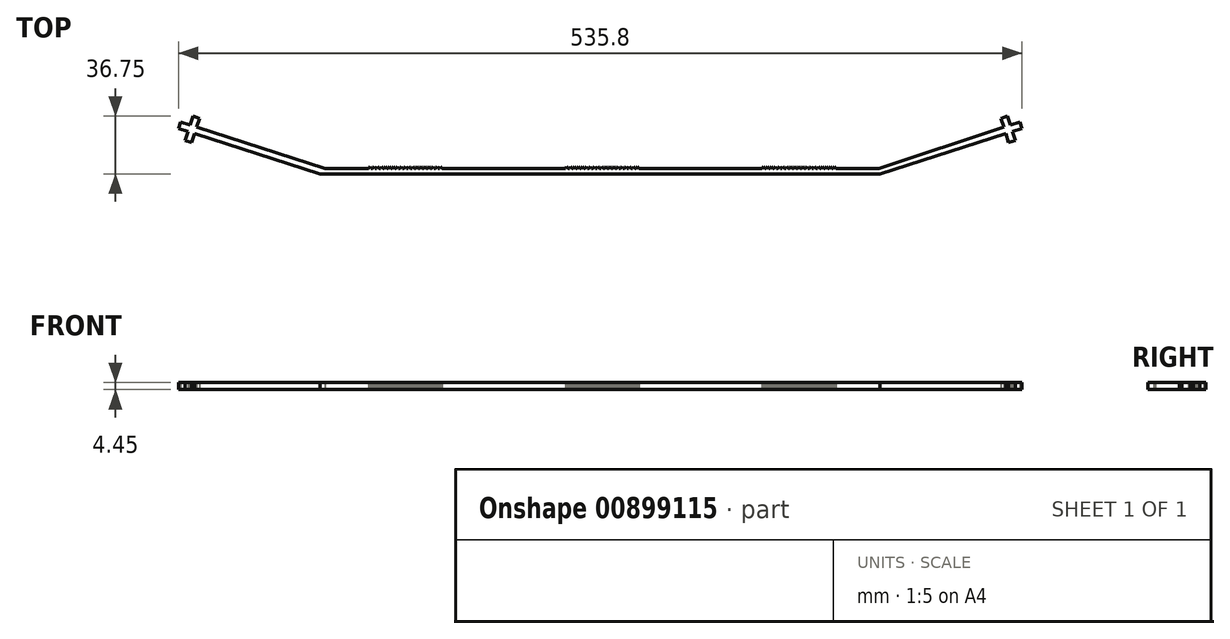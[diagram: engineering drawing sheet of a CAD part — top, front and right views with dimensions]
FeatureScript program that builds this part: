
annotation { "Feature Type Name" : "Feature", "Feature Type Description" : "" }
export const myFeature = defineFeature(function(context is Context, id is Id, definition is map)
    precondition{}
    {
        {
            var Q0;
            Q0=qCreatedBy(makeId("Top.planeOp"),FACE);
            var sketch = newSketch(context, id + "F0", { "sketchPlane" : qUnion([Q0])});
            skLineSegment(sketch, "E0", {"start": v(-253.44, 7.28) * mm, "end": v(102.16, 7.28) * mm});
            skLineSegment(sketch, "E1", {"start": v(-253.44, 7.28) * mm, "end": v(-333.25, 32.88) * mm});
            skLineSegment(sketch, "E2", {"start": v(-333.25, 32.88) * mm, "end": v(-335.04, 27.33) * mm});
            skLineSegment(sketch, "E3", {"start": v(-335.04, 27.33) * mm, "end": v(-339.27, 28.69) * mm});
            skLineSegment(sketch, "E4", {"start": v(-339.27, 28.69) * mm, "end": v(-337.5, 34.24) * mm});
            skLineSegment(sketch, "E5", {"start": v(-337.5, 34.24) * mm, "end": v(-343.54, 36.18) * mm});
            skLineSegment(sketch, "E6", {"start": v(-343.54, 36.18) * mm, "end": v(-342.18, 40.42) * mm});
            skLineSegment(sketch, "E7", {"start": v(-342.18, 40.42) * mm, "end": v(-336.13, 38.48) * mm});
            skLineSegment(sketch, "E8", {"start": v(-336.13, 38.48) * mm, "end": v(-334.35, 44.03) * mm});
            skLineSegment(sketch, "E9", {"start": v(-334.35, 44.03) * mm, "end": v(-330.11, 42.67) * mm});
            skLineSegment(sketch, "E10", {"start": v(-330.11, 42.67) * mm, "end": v(-331.9, 37.12) * mm});
            skLineSegment(sketch, "E11", {"start": v(-331.9, 37.12) * mm, "end": v(-252.08, 11.52) * mm});
            skLineSegment(sketch, "E12", {"start": v(-250.27, 10.94) * mm, "end": v(-222.78, 10.94) * mm});
            skLineSegment(sketch, "E13", {"start": v(-74.41, 12.08) * mm, "end": v(-73.54, 10.94) * mm});
            skLineSegment(sketch, "E14.MirrorCS", {"start": v(-74.41, 12.08) * mm, "end": v(-75.28, 10.94) * mm});
            skLineSegment(sketch, "E15.trimOffspring", {"start": v(-73.54, 10.94) * mm, "end": v(-72.78, 10.94) * mm});
            skPoint(sketch, "E16.start.orphan", {"position": v(-74.41, 4.9) * mm});
            skLineSegment(sketch, "E17.direction1", {"start": v(-73.54, 10.94) * mm, "end": v(-72.78, 10.94) * mm, "construction": true});
            skLineSegment(sketch, "E18.1.0.0", {"start": v(-71.91, 12.08) * mm, "end": v(-71.04, 10.94) * mm});
            skLineSegment(sketch, "E18.1.0.1", {"start": v(-71.91, 12.08) * mm, "end": v(-72.78, 10.94) * mm});
            skLineSegment(sketch, "E18.2.0.0", {"start": v(-69.41, 12.08) * mm, "end": v(-68.54, 10.94) * mm});
            skLineSegment(sketch, "E18.2.0.1", {"start": v(-69.41, 12.08) * mm, "end": v(-70.28, 10.94) * mm});
            skLineSegment(sketch, "E18.3.0.0", {"start": v(-66.91, 12.08) * mm, "end": v(-66.04, 10.94) * mm});
            skLineSegment(sketch, "E18.3.0.1", {"start": v(-66.91, 12.08) * mm, "end": v(-67.78, 10.94) * mm});
            skLineSegment(sketch, "E18.4.0.0", {"start": v(-64.41, 12.08) * mm, "end": v(-63.54, 10.94) * mm});
            skLineSegment(sketch, "E18.4.0.1", {"start": v(-64.41, 12.08) * mm, "end": v(-65.28, 10.94) * mm});
            skLineSegment(sketch, "E18.5.0.0", {"start": v(-61.91, 12.08) * mm, "end": v(-61.04, 10.94) * mm});
            skLineSegment(sketch, "E18.5.0.1", {"start": v(-61.91, 12.08) * mm, "end": v(-62.78, 10.94) * mm});
            skLineSegment(sketch, "E18.6.0.0", {"start": v(-59.41, 12.08) * mm, "end": v(-58.54, 10.94) * mm});
            skLineSegment(sketch, "E18.6.0.1", {"start": v(-59.41, 12.08) * mm, "end": v(-60.28, 10.94) * mm});
            skLineSegment(sketch, "E18.7.0.0", {"start": v(-56.91, 12.08) * mm, "end": v(-56.04, 10.94) * mm});
            skLineSegment(sketch, "E18.7.0.1", {"start": v(-56.91, 12.08) * mm, "end": v(-57.78, 10.94) * mm});
            skLineSegment(sketch, "E18.8.0.0", {"start": v(-54.41, 12.08) * mm, "end": v(-53.54, 10.94) * mm});
            skLineSegment(sketch, "E18.8.0.1", {"start": v(-54.41, 12.08) * mm, "end": v(-55.28, 10.94) * mm});
            skLineSegment(sketch, "E18.9.0.0", {"start": v(-51.91, 12.08) * mm, "end": v(-51.04, 10.94) * mm});
            skLineSegment(sketch, "E18.9.0.1", {"start": v(-51.91, 12.08) * mm, "end": v(-52.78, 10.94) * mm});
            skLineSegment(sketch, "E19.1.0.0", {"start": v(-76.91, 12.08) * mm, "end": v(-77.78, 10.94) * mm});
            skLineSegment(sketch, "E19.1.0.1", {"start": v(-76.91, 12.08) * mm, "end": v(-76.04, 10.94) * mm});
            skLineSegment(sketch, "E19.2.0.0", {"start": v(-79.41, 12.08) * mm, "end": v(-80.28, 10.94) * mm});
            skLineSegment(sketch, "E19.2.0.1", {"start": v(-79.41, 12.08) * mm, "end": v(-78.54, 10.94) * mm});
            skLineSegment(sketch, "E19.3.0.0", {"start": v(-81.91, 12.08) * mm, "end": v(-82.78, 10.94) * mm});
            skLineSegment(sketch, "E19.3.0.1", {"start": v(-81.91, 12.08) * mm, "end": v(-81.04, 10.94) * mm});
            skLineSegment(sketch, "E19.4.0.0", {"start": v(-84.41, 12.08) * mm, "end": v(-85.28, 10.94) * mm});
            skLineSegment(sketch, "E19.4.0.1", {"start": v(-84.41, 12.08) * mm, "end": v(-83.54, 10.94) * mm});
            skLineSegment(sketch, "E19.5.0.0", {"start": v(-86.91, 12.08) * mm, "end": v(-87.78, 10.94) * mm});
            skLineSegment(sketch, "E19.5.0.1", {"start": v(-86.91, 12.08) * mm, "end": v(-86.04, 10.94) * mm});
            skLineSegment(sketch, "E19.6.0.0", {"start": v(-89.41, 12.08) * mm, "end": v(-90.28, 10.94) * mm});
            skLineSegment(sketch, "E19.6.0.1", {"start": v(-89.41, 12.08) * mm, "end": v(-88.54, 10.94) * mm});
            skLineSegment(sketch, "E19.7.0.0", {"start": v(-91.91, 12.08) * mm, "end": v(-92.78, 10.94) * mm});
            skLineSegment(sketch, "E19.7.0.1", {"start": v(-91.91, 12.08) * mm, "end": v(-91.04, 10.94) * mm});
            skLineSegment(sketch, "E19.8.0.0", {"start": v(-94.41, 12.08) * mm, "end": v(-95.28, 10.94) * mm});
            skLineSegment(sketch, "E19.8.0.1", {"start": v(-94.41, 12.08) * mm, "end": v(-93.54, 10.94) * mm});
            skLineSegment(sketch, "E19.9.0.0", {"start": v(-96.91, 12.08) * mm, "end": v(-97.78, 10.94) * mm});
            skLineSegment(sketch, "E19.9.0.1", {"start": v(-96.91, 12.08) * mm, "end": v(-96.04, 10.94) * mm});
            skLineSegment(sketch, "E19.direction1", {"start": v(-75.28, 10.94) * mm, "end": v(-76.04, 10.94) * mm, "construction": true});
            skLineSegment(sketch, "E20.trimOffspring", {"start": v(-96.04, 10.94) * mm, "end": v(-95.28, 10.94) * mm});
            skLineSegment(sketch, "E21.trimOffspring", {"start": v(-93.54, 10.94) * mm, "end": v(-92.78, 10.94) * mm});
            skLineSegment(sketch, "E22.trimOffspring", {"start": v(-91.04, 10.94) * mm, "end": v(-90.28, 10.94) * mm});
            skLineSegment(sketch, "E23.trimOffspring", {"start": v(-86.04, 10.94) * mm, "end": v(-85.28, 10.94) * mm});
            skLineSegment(sketch, "E24.trimOffspring", {"start": v(-88.54, 10.94) * mm, "end": v(-87.78, 10.94) * mm});
            skLineSegment(sketch, "E25.trimOffspring", {"start": v(-83.54, 10.94) * mm, "end": v(-82.78, 10.94) * mm});
            skLineSegment(sketch, "E26.trimOffspring", {"start": v(-81.04, 10.94) * mm, "end": v(-80.28, 10.94) * mm});
            skLineSegment(sketch, "E27.trimOffspring", {"start": v(-78.54, 10.94) * mm, "end": v(-77.78, 10.94) * mm});
            skLineSegment(sketch, "E28.trimOffspring", {"start": v(-76.04, 10.94) * mm, "end": v(-75.28, 10.94) * mm});
            skLineSegment(sketch, "E29.trimOffspring", {"start": v(-71.04, 10.94) * mm, "end": v(-70.28, 10.94) * mm, "construction": true});
            skLineSegment(sketch, "E30.trimOffspring", {"start": v(-71.04, 10.94) * mm, "end": v(-70.28, 10.94) * mm});
            skLineSegment(sketch, "E31.trimOffspring", {"start": v(-68.54, 10.94) * mm, "end": v(-67.78, 10.94) * mm, "construction": true});
            skLineSegment(sketch, "E32.trimOffspring", {"start": v(-68.54, 10.94) * mm, "end": v(-67.78, 10.94) * mm});
            skLineSegment(sketch, "E33.trimOffspring", {"start": v(-66.04, 10.94) * mm, "end": v(-65.28, 10.94) * mm, "construction": true});
            skLineSegment(sketch, "E34.trimOffspring", {"start": v(-63.54, 10.94) * mm, "end": v(-62.78, 10.94) * mm, "construction": true});
            skLineSegment(sketch, "E35.trimOffspring", {"start": v(-63.54, 10.94) * mm, "end": v(-62.78, 10.94) * mm});
            skLineSegment(sketch, "E36", {"start": v(-66.04, 10.94) * mm, "end": v(-65.28, 10.94) * mm});
            skLineSegment(sketch, "E37.trimOffspring", {"start": v(-61.04, 10.94) * mm, "end": v(-60.28, 10.94) * mm, "construction": true});
            skLineSegment(sketch, "E38.trimOffspring", {"start": v(-61.04, 10.94) * mm, "end": v(-60.28, 10.94) * mm});
            skLineSegment(sketch, "E39.trimOffspring", {"start": v(-58.54, 10.94) * mm, "end": v(-57.78, 10.94) * mm, "construction": true});
            skLineSegment(sketch, "E40.trimOffspring", {"start": v(-58.54, 10.94) * mm, "end": v(-57.78, 10.94) * mm});
            skLineSegment(sketch, "E41.trimOffspring", {"start": v(-56.04, 10.94) * mm, "end": v(-55.28, 10.94) * mm, "construction": true});
            skLineSegment(sketch, "E42.trimOffspring", {"start": v(-56.04, 10.94) * mm, "end": v(-55.28, 10.94) * mm});
            skLineSegment(sketch, "E43.trimOffspring", {"start": v(-53.54, 10.94) * mm, "end": v(-52.78, 10.94) * mm, "construction": true});
            skLineSegment(sketch, "E44.trimOffspring", {"start": v(-53.54, 10.94) * mm, "end": v(-52.78, 10.94) * mm});
            skLineSegment(sketch, "E45.trimOffspring", {"start": v(-51.04, 10.94) * mm, "end": v(-48.54, 10.94) * mm, "construction": true});
            skLineSegment(sketch, "E46.trimOffspring", {"start": v(-51.04, 10.94) * mm, "end": v(27.22, 10.94) * mm});
            skLineSegment(sketch, "E47.1.0.0", {"start": v(73.09, 12.08) * mm, "end": v(73.96, 10.94) * mm});
            skLineSegment(sketch, "E47.1.0.1", {"start": v(73.09, 12.08) * mm, "end": v(72.22, 10.94) * mm});
            skLineSegment(sketch, "E47.1.0.2", {"start": v(70.59, 12.08) * mm, "end": v(71.46, 10.94) * mm});
            skLineSegment(sketch, "E47.1.0.3", {"start": v(70.59, 12.08) * mm, "end": v(69.72, 10.94) * mm});
            skLineSegment(sketch, "E47.1.0.4", {"start": v(68.09, 12.08) * mm, "end": v(68.96, 10.94) * mm});
            skLineSegment(sketch, "E47.1.0.5", {"start": v(68.09, 12.08) * mm, "end": v(67.22, 10.94) * mm});
            skLineSegment(sketch, "E47.1.0.6", {"start": v(65.59, 12.08) * mm, "end": v(66.46, 10.94) * mm});
            skLineSegment(sketch, "E47.1.0.7", {"start": v(65.59, 12.08) * mm, "end": v(64.72, 10.94) * mm});
            skLineSegment(sketch, "E47.1.0.8", {"start": v(63.09, 12.08) * mm, "end": v(63.96, 10.94) * mm});
            skLineSegment(sketch, "E47.1.0.9", {"start": v(63.09, 12.08) * mm, "end": v(62.22, 10.94) * mm});
            skLineSegment(sketch, "E47.1.0.10", {"start": v(60.59, 12.08) * mm, "end": v(61.46, 10.94) * mm});
            skLineSegment(sketch, "E47.1.0.11", {"start": v(60.59, 12.08) * mm, "end": v(59.72, 10.94) * mm});
            skLineSegment(sketch, "E47.1.0.12", {"start": v(58.09, 12.08) * mm, "end": v(58.96, 10.94) * mm});
            skLineSegment(sketch, "E47.1.0.13", {"start": v(58.09, 12.08) * mm, "end": v(57.22, 10.94) * mm});
            skLineSegment(sketch, "E47.1.0.14", {"start": v(55.59, 12.08) * mm, "end": v(56.46, 10.94) * mm});
            skLineSegment(sketch, "E47.1.0.15", {"start": v(55.59, 12.08) * mm, "end": v(54.72, 10.94) * mm});
            skLineSegment(sketch, "E47.1.0.16", {"start": v(53.09, 12.08) * mm, "end": v(53.96, 10.94) * mm});
            skLineSegment(sketch, "E47.1.0.17", {"start": v(53.09, 12.08) * mm, "end": v(52.22, 10.94) * mm});
            skLineSegment(sketch, "E47.1.0.18", {"start": v(50.59, 12.08) * mm, "end": v(51.46, 10.94) * mm});
            skLineSegment(sketch, "E47.1.0.19", {"start": v(50.59, 12.08) * mm, "end": v(49.72, 10.94) * mm});
            skLineSegment(sketch, "E47.1.0.20", {"start": v(48.09, 12.08) * mm, "end": v(48.96, 10.94) * mm});
            skLineSegment(sketch, "E47.1.0.21", {"start": v(48.09, 12.08) * mm, "end": v(47.22, 10.94) * mm});
            skLineSegment(sketch, "E47.1.0.22", {"start": v(45.59, 12.08) * mm, "end": v(46.46, 10.94) * mm});
            skLineSegment(sketch, "E47.1.0.23", {"start": v(45.59, 12.08) * mm, "end": v(44.72, 10.94) * mm});
            skLineSegment(sketch, "E47.1.0.24", {"start": v(43.09, 12.08) * mm, "end": v(43.96, 10.94) * mm});
            skLineSegment(sketch, "E47.1.0.25", {"start": v(43.09, 12.08) * mm, "end": v(42.22, 10.94) * mm});
            skLineSegment(sketch, "E47.1.0.26", {"start": v(40.59, 12.08) * mm, "end": v(41.46, 10.94) * mm});
            skLineSegment(sketch, "E47.1.0.27", {"start": v(40.59, 12.08) * mm, "end": v(39.72, 10.94) * mm});
            skLineSegment(sketch, "E47.1.0.28", {"start": v(38.09, 12.08) * mm, "end": v(38.96, 10.94) * mm});
            skLineSegment(sketch, "E47.1.0.29", {"start": v(38.09, 12.08) * mm, "end": v(37.22, 10.94) * mm});
            skLineSegment(sketch, "E47.1.0.30", {"start": v(35.59, 12.08) * mm, "end": v(36.46, 10.94) * mm});
            skLineSegment(sketch, "E47.1.0.31", {"start": v(35.59, 12.08) * mm, "end": v(34.72, 10.94) * mm});
            skLineSegment(sketch, "E47.1.0.32", {"start": v(33.09, 12.08) * mm, "end": v(33.96, 10.94) * mm});
            skLineSegment(sketch, "E47.1.0.33", {"start": v(33.09, 12.08) * mm, "end": v(32.22, 10.94) * mm});
            skLineSegment(sketch, "E47.1.0.34", {"start": v(30.59, 12.08) * mm, "end": v(31.46, 10.94) * mm});
            skLineSegment(sketch, "E47.1.0.35", {"start": v(30.59, 12.08) * mm, "end": v(29.72, 10.94) * mm});
            skLineSegment(sketch, "E47.1.0.36", {"start": v(28.09, 12.08) * mm, "end": v(28.96, 10.94) * mm});
            skLineSegment(sketch, "E47.1.0.37", {"start": v(28.09, 12.08) * mm, "end": v(27.22, 10.94) * mm});
            skLineSegment(sketch, "E48.1.0.0", {"start": v(-176.91, 12.08) * mm, "end": v(-176.04, 10.94) * mm});
            skLineSegment(sketch, "E48.1.0.1", {"start": v(-176.91, 12.08) * mm, "end": v(-177.78, 10.94) * mm});
            skLineSegment(sketch, "E48.1.0.2", {"start": v(-179.41, 12.08) * mm, "end": v(-178.54, 10.94) * mm});
            skLineSegment(sketch, "E48.1.0.3", {"start": v(-179.41, 12.08) * mm, "end": v(-180.28, 10.94) * mm});
            skLineSegment(sketch, "E48.1.0.4", {"start": v(-181.91, 12.08) * mm, "end": v(-181.04, 10.94) * mm});
            skLineSegment(sketch, "E48.1.0.5", {"start": v(-181.91, 12.08) * mm, "end": v(-182.78, 10.94) * mm});
            skLineSegment(sketch, "E48.1.0.6", {"start": v(-184.41, 12.08) * mm, "end": v(-183.54, 10.94) * mm});
            skLineSegment(sketch, "E48.1.0.7", {"start": v(-184.41, 12.08) * mm, "end": v(-185.28, 10.94) * mm});
            skLineSegment(sketch, "E48.1.0.8", {"start": v(-186.91, 12.08) * mm, "end": v(-186.04, 10.94) * mm});
            skLineSegment(sketch, "E48.1.0.9", {"start": v(-186.91, 12.08) * mm, "end": v(-187.78, 10.94) * mm});
            skLineSegment(sketch, "E48.1.0.10", {"start": v(-189.41, 12.08) * mm, "end": v(-188.54, 10.94) * mm});
            skLineSegment(sketch, "E48.1.0.11", {"start": v(-189.41, 12.08) * mm, "end": v(-190.28, 10.94) * mm});
            skLineSegment(sketch, "E48.1.0.12", {"start": v(-191.91, 12.08) * mm, "end": v(-191.04, 10.94) * mm});
            skLineSegment(sketch, "E48.1.0.13", {"start": v(-191.91, 12.08) * mm, "end": v(-192.78, 10.94) * mm});
            skLineSegment(sketch, "E48.1.0.14", {"start": v(-194.41, 12.08) * mm, "end": v(-193.54, 10.94) * mm});
            skLineSegment(sketch, "E48.1.0.15", {"start": v(-194.41, 12.08) * mm, "end": v(-195.28, 10.94) * mm});
            skLineSegment(sketch, "E48.1.0.16", {"start": v(-196.91, 12.08) * mm, "end": v(-196.04, 10.94) * mm});
            skLineSegment(sketch, "E48.1.0.17", {"start": v(-196.91, 12.08) * mm, "end": v(-197.78, 10.94) * mm});
            skLineSegment(sketch, "E48.1.0.18", {"start": v(-199.41, 12.08) * mm, "end": v(-198.54, 10.94) * mm});
            skLineSegment(sketch, "E48.1.0.19", {"start": v(-199.41, 12.08) * mm, "end": v(-200.28, 10.94) * mm});
            skLineSegment(sketch, "E48.1.0.20", {"start": v(-221.91, 12.08) * mm, "end": v(-222.78, 10.94) * mm});
            skLineSegment(sketch, "E48.1.0.21", {"start": v(-221.91, 12.08) * mm, "end": v(-221.04, 10.94) * mm});
            skLineSegment(sketch, "E48.1.0.22", {"start": v(-219.41, 12.08) * mm, "end": v(-220.28, 10.94) * mm});
            skLineSegment(sketch, "E48.1.0.23", {"start": v(-219.41, 12.08) * mm, "end": v(-218.54, 10.94) * mm});
            skLineSegment(sketch, "E48.1.0.24", {"start": v(-216.91, 12.08) * mm, "end": v(-217.78, 10.94) * mm});
            skLineSegment(sketch, "E48.1.0.25", {"start": v(-216.91, 12.08) * mm, "end": v(-216.04, 10.94) * mm});
            skLineSegment(sketch, "E48.1.0.26", {"start": v(-214.41, 12.08) * mm, "end": v(-215.28, 10.94) * mm});
            skLineSegment(sketch, "E48.1.0.27", {"start": v(-214.41, 12.08) * mm, "end": v(-213.54, 10.94) * mm});
            skLineSegment(sketch, "E48.1.0.28", {"start": v(-211.91, 12.08) * mm, "end": v(-212.78, 10.94) * mm});
            skLineSegment(sketch, "E48.1.0.29", {"start": v(-211.91, 12.08) * mm, "end": v(-211.04, 10.94) * mm});
            skLineSegment(sketch, "E48.1.0.30", {"start": v(-209.41, 12.08) * mm, "end": v(-210.28, 10.94) * mm});
            skLineSegment(sketch, "E48.1.0.31", {"start": v(-209.41, 12.08) * mm, "end": v(-208.54, 10.94) * mm});
            skLineSegment(sketch, "E48.1.0.32", {"start": v(-206.91, 12.08) * mm, "end": v(-207.78, 10.94) * mm});
            skLineSegment(sketch, "E48.1.0.33", {"start": v(-206.91, 12.08) * mm, "end": v(-206.04, 10.94) * mm});
            skLineSegment(sketch, "E48.1.0.34", {"start": v(-204.41, 12.08) * mm, "end": v(-205.28, 10.94) * mm});
            skLineSegment(sketch, "E48.1.0.35", {"start": v(-204.41, 12.08) * mm, "end": v(-203.54, 10.94) * mm});
            skLineSegment(sketch, "E48.1.0.36", {"start": v(-201.91, 12.08) * mm, "end": v(-202.78, 10.94) * mm});
            skLineSegment(sketch, "E48.1.0.37", {"start": v(-201.91, 12.08) * mm, "end": v(-201.04, 10.94) * mm});
            skLineSegment(sketch, "E48.direction1", {"start": v(-51.04, 10.94) * mm, "end": v(-176.04, 10.94) * mm, "construction": true});
            skLineSegment(sketch, "E49.trimOffspring", {"start": v(-221.04, 10.94) * mm, "end": v(-220.28, 10.94) * mm});
            skLineSegment(sketch, "E50.trimOffspring", {"start": v(-218.54, 10.94) * mm, "end": v(-217.78, 10.94) * mm});
            skLineSegment(sketch, "E51.trimOffspring", {"start": v(-216.04, 10.94) * mm, "end": v(-215.28, 10.94) * mm});
            skLineSegment(sketch, "E52.trimOffspring", {"start": v(-213.54, 10.94) * mm, "end": v(-212.78, 10.94) * mm});
            skLineSegment(sketch, "E53.trimOffspring", {"start": v(-211.04, 10.94) * mm, "end": v(-210.28, 10.94) * mm});
            skLineSegment(sketch, "E54.trimOffspring", {"start": v(-208.54, 10.94) * mm, "end": v(-207.78, 10.94) * mm});
            skLineSegment(sketch, "E55.trimOffspring", {"start": v(-206.04, 10.94) * mm, "end": v(-205.28, 10.94) * mm});
            skLineSegment(sketch, "E56.trimOffspring", {"start": v(-203.54, 10.94) * mm, "end": v(-202.78, 10.94) * mm});
            skLineSegment(sketch, "E57.trimOffspring", {"start": v(-201.04, 10.94) * mm, "end": v(-200.28, 10.94) * mm});
            skLineSegment(sketch, "E58.trimOffspring", {"start": v(-198.54, 10.94) * mm, "end": v(-197.78, 10.94) * mm});
            skLineSegment(sketch, "E59.trimOffspring", {"start": v(-196.04, 10.94) * mm, "end": v(-195.28, 10.94) * mm});
            skLineSegment(sketch, "E60.trimOffspring", {"start": v(-193.54, 10.94) * mm, "end": v(-192.78, 10.94) * mm});
            skLineSegment(sketch, "E61.trimOffspring", {"start": v(-191.04, 10.94) * mm, "end": v(-190.28, 10.94) * mm});
            skLineSegment(sketch, "E62.trimOffspring", {"start": v(-188.54, 10.94) * mm, "end": v(-187.78, 10.94) * mm});
            skLineSegment(sketch, "E63.trimOffspring", {"start": v(-186.04, 10.94) * mm, "end": v(-185.28, 10.94) * mm});
            skLineSegment(sketch, "E64.trimOffspring", {"start": v(-183.54, 10.94) * mm, "end": v(-182.78, 10.94) * mm});
            skLineSegment(sketch, "E65.trimOffspring", {"start": v(-181.04, 10.94) * mm, "end": v(-180.28, 10.94) * mm});
            skLineSegment(sketch, "E66.trimOffspring", {"start": v(-178.54, 10.94) * mm, "end": v(-177.78, 10.94) * mm});
            skLineSegment(sketch, "E67.trimOffspring", {"start": v(-176.04, 10.94) * mm, "end": v(-97.78, 10.94) * mm});
            skLineSegment(sketch, "E68.trimOffspring", {"start": v(73.96, 10.94) * mm, "end": v(101.45, 10.94) * mm});
            skLineSegment(sketch, "E69.trimOffspring", {"start": v(71.46, 10.94) * mm, "end": v(72.22, 10.94) * mm, "construction": true});
            skLineSegment(sketch, "E70.trimOffspring", {"start": v(71.46, 10.94) * mm, "end": v(72.22, 10.94) * mm});
            skLineSegment(sketch, "E71.trimOffspring", {"start": v(68.96, 10.94) * mm, "end": v(69.72, 10.94) * mm, "construction": true});
            skLineSegment(sketch, "E72.trimOffspring", {"start": v(68.96, 10.94) * mm, "end": v(69.72, 10.94) * mm});
            skLineSegment(sketch, "E73.trimOffspring", {"start": v(66.46, 10.94) * mm, "end": v(67.22, 10.94) * mm, "construction": true});
            skLineSegment(sketch, "E74.trimOffspring", {"start": v(66.46, 10.94) * mm, "end": v(67.22, 10.94) * mm});
            skLineSegment(sketch, "E75.trimOffspring", {"start": v(63.96, 10.94) * mm, "end": v(64.72, 10.94) * mm, "construction": true});
            skLineSegment(sketch, "E76.trimOffspring", {"start": v(63.96, 10.94) * mm, "end": v(64.72, 10.94) * mm});
            skLineSegment(sketch, "E77.trimOffspring", {"start": v(61.46, 10.94) * mm, "end": v(62.22, 10.94) * mm});
            skLineSegment(sketch, "E78.trimOffspring", {"start": v(58.96, 10.94) * mm, "end": v(59.72, 10.94) * mm});
            skLineSegment(sketch, "E79.trimOffspring", {"start": v(56.46, 10.94) * mm, "end": v(57.22, 10.94) * mm});
            skLineSegment(sketch, "E80.trimOffspring", {"start": v(53.96, 10.94) * mm, "end": v(54.72, 10.94) * mm});
            skLineSegment(sketch, "E81.trimOffspring", {"start": v(51.46, 10.94) * mm, "end": v(52.22, 10.94) * mm});
            skLineSegment(sketch, "E82.trimOffspring", {"start": v(48.96, 10.94) * mm, "end": v(49.72, 10.94) * mm});
            skLineSegment(sketch, "E83.trimOffspring", {"start": v(46.46, 10.94) * mm, "end": v(47.22, 10.94) * mm});
            skLineSegment(sketch, "E84.trimOffspring", {"start": v(43.96, 10.94) * mm, "end": v(44.72, 10.94) * mm});
            skLineSegment(sketch, "E85.trimOffspring", {"start": v(28.96, 10.94) * mm, "end": v(29.72, 10.94) * mm});
            skLineSegment(sketch, "E86.trimOffspring", {"start": v(31.46, 10.94) * mm, "end": v(32.22, 10.94) * mm});
            skLineSegment(sketch, "E87.trimOffspring", {"start": v(33.96, 10.94) * mm, "end": v(34.72, 10.94) * mm});
            skLineSegment(sketch, "E88.trimOffspring", {"start": v(36.46, 10.94) * mm, "end": v(37.22, 10.94) * mm});
            skLineSegment(sketch, "E89.trimOffspring", {"start": v(38.96, 10.94) * mm, "end": v(39.72, 10.94) * mm});
            skLineSegment(sketch, "E90.trimOffspring", {"start": v(41.46, 10.94) * mm, "end": v(42.22, 10.94) * mm});
            skLineSegment(sketch, "E91", {"start": v(-252.08, 11.52) * mm, "end": v(-250.27, 10.94) * mm});
            skLineSegment(sketch, "E92.MirrorCS", {"start": v(192.26, 36.18) * mm, "end": v(190.9, 40.42) * mm});
            skLineSegment(sketch, "E93.MirrorCS", {"start": v(183.76, 27.33) * mm, "end": v(188, 28.69) * mm});
            skLineSegment(sketch, "E94.MirrorCS", {"start": v(183.07, 44.03) * mm, "end": v(178.84, 42.67) * mm});
            skLineSegment(sketch, "E95.MirrorCS", {"start": v(186.21, 34.24) * mm, "end": v(192.26, 36.18) * mm});
            skLineSegment(sketch, "E96.MirrorCS", {"start": v(184.85, 38.48) * mm, "end": v(183.07, 44.03) * mm});
            skLineSegment(sketch, "E97.MirrorCS", {"start": v(190.9, 40.42) * mm, "end": v(184.85, 38.48) * mm});
            skLineSegment(sketch, "E98.MirrorCS", {"start": v(181.98, 32.88) * mm, "end": v(183.76, 27.33) * mm});
            skLineSegment(sketch, "E99.MirrorCS", {"start": v(188, 28.69) * mm, "end": v(186.21, 34.24) * mm});
            skLineSegment(sketch, "E100.MirrorCS", {"start": v(178.84, 42.67) * mm, "end": v(180.62, 37.12) * mm});
            skLineSegment(sketch, "E101.MirrorCS", {"start": v(102.16, 7.28) * mm, "end": v(181.98, 32.88) * mm});
            skLineSegment(sketch, "E102.MirrorCS", {"start": v(180.62, 37.12) * mm, "end": v(101.45, 10.94) * mm});
            skSolve(sketch);
        }
        {
            var Q0;
            Q0=makeQuery(id+"F0.imprint","IMPRINT",FACE,{"disambiguationData":[TD([[makeQuery(id+"F0.imprint","IMPRINT",EDGE,{"derivedFrom":sQuery(id+"F0.wireOp",EDGE,"E0")}),1.0]])]});
            extrude(context, id + "F1", {"entities" : qUnion([Q0]), "depth" : 4.45 * mm, "offsetDistance" : 25 * mm});
        }
    });
